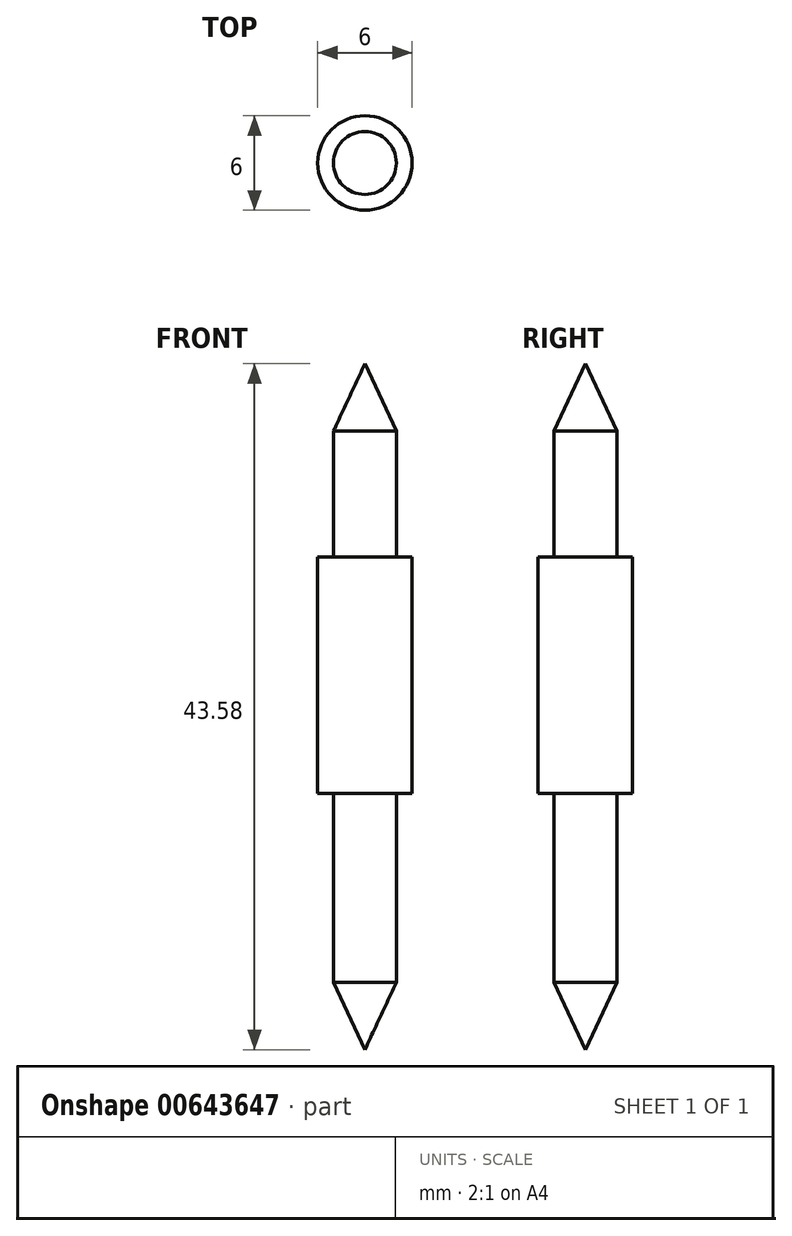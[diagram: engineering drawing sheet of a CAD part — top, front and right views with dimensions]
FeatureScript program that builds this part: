
annotation { "Feature Type Name" : "Feature", "Feature Type Description" : "" }
export const myFeature = defineFeature(function(context is Context, id is Id, definition is map)
    precondition{}
    {
        {
            var Q0;
            Q0=qCreatedBy(makeId("Front.planeOp"),FACE);
            var sketch = newSketch(context, id + "F0", { "sketchPlane" : qUnion([Q0])});
            skLineSegment(sketch, "E0", {"start": v(0, 0) * mm, "end": v(-2, 4.29) * mm});
            skLineSegment(sketch, "E1", {"start": v(-2, 4.29) * mm, "end": v(-2, 16.29) * mm});
            skLineSegment(sketch, "E2", {"start": v(-2, 39.29) * mm, "end": v(0, 43.58) * mm});
            skLineSegment(sketch, "E3", {"start": v(0, 43.58) * mm, "end": v(0, 0) * mm});
            skLineSegment(sketch, "E4", {"start": v(-2, 16.29) * mm, "end": v(-3, 16.29) * mm});
            skLineSegment(sketch, "E5", {"start": v(-3, 16.29) * mm, "end": v(-3, 31.29) * mm});
            skLineSegment(sketch, "E6", {"start": v(-3, 31.29) * mm, "end": v(-2, 31.29) * mm});
            skLineSegment(sketch, "E7.trimOffspring", {"start": v(-2, 31.29) * mm, "end": v(-2, 39.29) * mm});
            skSolve(sketch);
        }
        {
            var Q0;
            Q0 = qSketchRegion(id + "F0", true);
            var Q1;
            Q1=sQuery(id+"F0.wireOp",EDGE,"E3");
            revolve(context, id + "F1", {"entities" : qUnion([Q0]), "axis" : qUnion([Q1]), "revolveType" : RevolveType.FULL});
        }
    });
